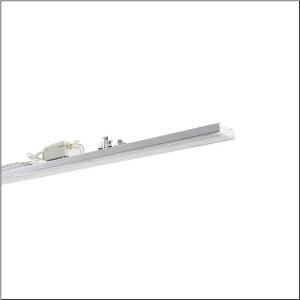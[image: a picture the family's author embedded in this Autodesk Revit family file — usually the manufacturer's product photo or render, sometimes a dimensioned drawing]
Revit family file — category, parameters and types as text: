
# Revit family: licross_11_recessed_mo_51te12dv4fxg3s4
name_source: partatom
category: Lighting Fixtures
units: mm (PartAtom-declared; Revit-internal decimal feet)

## family parameters
Cut with Voids When Loaded = No
Host = Face
Light Source = No
Part Type = Normal
Room Calculation Point = No
Round Connector Dimension = Use Diameter
Shared = No

## types (1)
- --- (1 x LED, 1010 lm, 5.5 W, 4000K)
    Apparent Load = 6 VA
    CIE Flux Codes = 67 92 99 100 100
    Color Rendering = 80
    Color Temperature = 4000K
    Default Elevation = 1800 mm
    Description = Licross 11 Recessed MO, luminaire insert, of sheet steel, galvanised, coil coated, white, length: 2.250mm, width: 66mm, height: 67mm, LED rated luminous flux: 15.360lm, light colour: 840, SDCM (Standard Deviation of Colour Matching)MacAdam ≤ 2 SDCM (initial), control gear: DALI 2, with plug, 6-pole, with phase selection, for trunking rail, 9 or 11-core, mains connection: 220..240V, AC, 50/60Hz, rated input power: 88W, for trunking rail, 9-/11-core, internal wiring halogen-free, for emergency light function, converter,control gear: single battery element, battery: LiFePO4, 9Ah, primary optical cover: cover, of PMMA, light emission: direct distribution, primary light characteristic: symmetric, protection rating (complete): IP54, insulation class (complete): insulation class I (protective earthing), certification: CE, UKCA, protection symbol: D if used in an environment with non-conductive dust loads with corresponding accessories, impact resistance: IK06, permissible ambient temperature for indoor applications: +5..+35°C, standard: EN 60598-2-22, LABS conformity tested according to VDMA 24364:2018-05, reducing of maximum allowable ambient temperature of 5°C with ceiling mounting, corresponds to IFS (International Featured Standards) requirements for safety and quality in the food industry, The light source and the operating device comply with the requirements of the Ecodesign Regulation (EU) 2019/2020 and are replaceable in accordance with this regulation, packaging unit: 1 piece
    Height = 58 mm
    Lamp = 1 x LED
    Lamp Light Flux = 1010 lm
    Lamp Power = 5.5 W
    Lamp count = 1
    Length = 2250 mm
    Luminous efficacy = 184 lm/W
    Manufacturer = Siteco
    ModVariant = No
    Model = 51TE12DV4FXG3S4
    Mounting Place = Ceiling
    Mounting Type = Pendant
    Number of Poles = 1
    OnlyDefault = Yes
    Power Factor = 1
    Product Name = Licross 11 Recessed MO
    Product group = luminaire insert | ceiling pendant
    ProductGroupID = 901
    Protection Class = Protection class I
    Protection Degree = IP 54
    RLX_Detail_Level = 1
    RLX_Emergency_Light_Flux = 0 lm
    RLX_Emergency_Type = 0
    RLX_Emergency_Type_DB = No
    RlxData = <blob elided: 30141 chars, md5=bdfe4065>
    Socket = socket
    Standby Power = 0 W
    System Light Flux = 1010 lm
    System Power = 6 W
    Type Comments = : emergency light operation: 3 h
    Type Image = l_1296930.jpg
    URL = http://relux.com
    VarID = @adj_091571
    Voltage = 0 V
    Weight = 0.00 kg
    Width = 66 mm

## geometry (parser evidence)
native form markers: Blend x4, Sweep x12
no freeform markers — native parametric forms only
